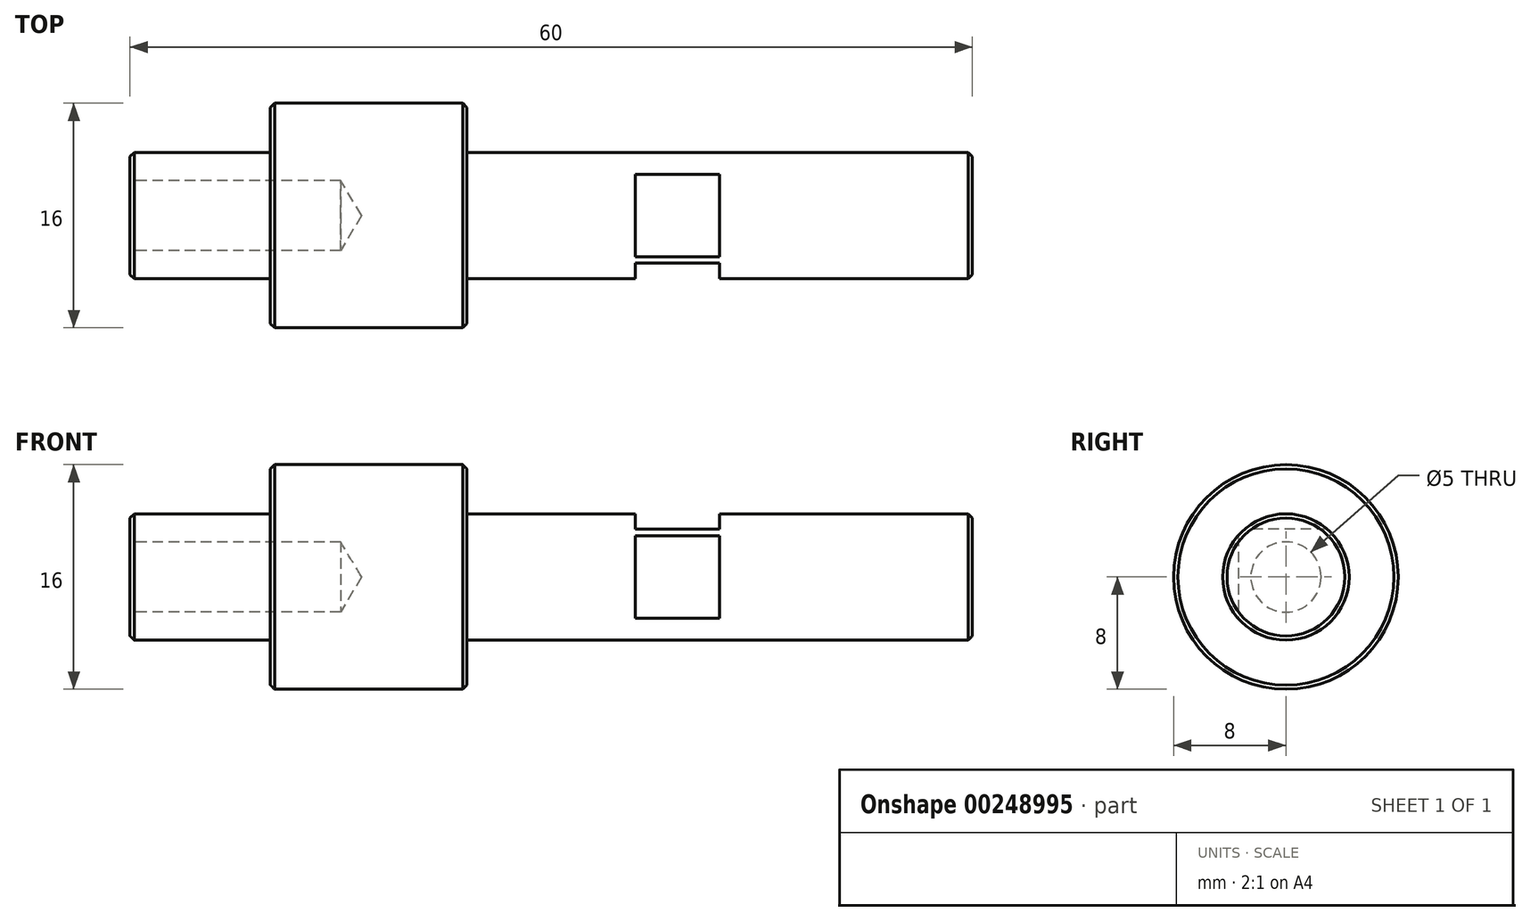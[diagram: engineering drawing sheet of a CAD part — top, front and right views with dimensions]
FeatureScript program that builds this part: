
annotation { "Feature Type Name" : "Feature", "Feature Type Description" : "" }
export const myFeature = defineFeature(function(context is Context, id is Id, definition is map)
    precondition{}
    {
        {
            var Q0;
            Q0=qCreatedBy(makeId("Front.planeOp"),FACE);
            var sketch = newSketch(context, id + "F0", { "sketchPlane" : qUnion([Q0])});
            skLineSegment(sketch, "E0", {"start": v(-26.32, 0) * mm, "end": v(33.68, 0) * mm});
            skLineSegment(sketch, "E1", {"start": v(33.68, 4.5) * mm, "end": v(33.68, 0) * mm});
            skLineSegment(sketch, "E2", {"start": v(33.68, 4.5) * mm, "end": v(-2.32, 4.5) * mm});
            skLineSegment(sketch, "E3", {"start": v(-2.32, 4.5) * mm, "end": v(-2.32, 8) * mm});
            skLineSegment(sketch, "E4", {"start": v(-2.32, 8) * mm, "end": v(-16.32, 8) * mm});
            skLineSegment(sketch, "E5", {"start": v(-16.32, 8) * mm, "end": v(-16.32, 4.5) * mm});
            skLineSegment(sketch, "E6", {"start": v(-16.32, 4.5) * mm, "end": v(-26.32, 4.5) * mm});
            skLineSegment(sketch, "E7", {"start": v(-26.32, 4.5) * mm, "end": v(-26.32, 0) * mm});
            skSolve(sketch);
        }
        {
            var Q0;
            Q0=makeQuery(id+"F0.imprint","IMPRINT",FACE,{"disambiguationData":[TD([[makeQuery(id+"F0.imprint","IMPRINT",EDGE,{"derivedFrom":sQuery(id+"F0.wireOp",EDGE,"E0")}),1.0]])]});
            var Q1;
            Q1=sQuery(id+"F0.wireOp",EDGE,"E0");
            revolve(context, id + "F1", {"entities" : qUnion([Q0]), "axis" : qUnion([Q1]), "revolveType" : RevolveType.FULL});
        }
        {
            var Q0;
            Q0=makeQuery(id+"F1.opRevolve","SWEPT_EDGE",EDGE,{"disambiguationData":[OSD([sQuery(id+"F0.wireOp",EDGE,"E1"),sQuery(id+"F0.wireOp",EDGE,"E2")])]});
            chamfer(context, id + "F2", {"entities" : qUnion([Q0]), "width" : .3 * mm, "tangentPropagation" : true});
        }
        {
            var Q0;
            Q0=makeQuery(id+"F1.opRevolve","SWEPT_FACE",FACE,{"disambiguationData":[OSD([sQuery(id+"F0.wireOp",EDGE,"E4")])]});
            chamfer(context, id + "F3", {"entities" : qUnion([Q0]), "width" : .3 * mm, "tangentPropagation" : true});
        }
        {
            var Q0;
            Q0=makeQuery(id+"F1.opRevolve","SWEPT_FACE",FACE,{"disambiguationData":[OSD([sQuery(id+"F0.wireOp",EDGE,"E7")])]});
            chamfer(context, id + "F4", {"entities" : qUnion([Q0]), "width" : .3 * mm, "tangentPropagation" : true});
        }
        {
            var Q0;
            Q0=qCreatedBy(makeId("Front.planeOp"),FACE);
            var sketch = newSketch(context, id + "F5", { "sketchPlane" : qUnion([Q0])});
            skLineSegment(sketch, "E8.bottom", {"start": v(15.68, 3) * mm, "end": v(9.68, 3) * mm});
            skLineSegment(sketch, "E8.top", {"start": v(15.68, -3) * mm, "end": v(9.68, -3) * mm});
            skLineSegment(sketch, "E8.left", {"start": v(15.68, 3) * mm, "end": v(15.68, -3) * mm});
            skLineSegment(sketch, "E8.right", {"start": v(9.68, 3) * mm, "end": v(9.68, -3) * mm});
            skPoint(sketch, "E8.middle", {"position": v(12.68, 0) * mm});
            skSolve(sketch);
        }
        {
            var Q0;
            Q0=qCreatedBy(makeId("Front.planeOp"),FACE);
            cPlane(context, id + "F6", {"entities" : qUnion([Q0]), "cplaneType" : CPlaneType.OFFSET, "offset" : 4.5 * mm, "width" : 150 * mm, "height" : 150 * mm});
        }
        {
            var Q0;
            Q0=qCreatedBy(id+"F6.planeOp",FACE);
            var sketch = newSketch(context, id + "F7", { "sketchPlane" : qUnion([Q0])});
            skPoint(sketch, "E9.0", {"position": v(15.68, 3) * mm});
            skPoint(sketch, "E10.0", {"position": v(12.68, 3) * mm});
            skLineSegment(sketch, "E11.0", {"start": v(15.68, 3) * mm, "end": v(9.68, 3) * mm});
            skPoint(sketch, "E12.0", {"position": v(9.68, 0) * mm});
            skLineSegment(sketch, "E13.0", {"start": v(15.68, -3) * mm, "end": v(9.68, -3) * mm});
            skLineSegment(sketch, "E14.0", {"start": v(15.68, 3) * mm, "end": v(15.68, -3) * mm});
            skLineSegment(sketch, "E15.0", {"start": v(9.68, 3) * mm, "end": v(9.68, -3) * mm});
            skSolve(sketch);
        }
        {
            var Q0;
            Q0=makeQuery(id+"F7.imprint","IMPRINT",FACE,{"disambiguationData":[TD([[makeQuery(id+"F7.imprint","IMPRINT",EDGE,{"derivedFrom":sQuery(id+"F7.wireOp",EDGE,"E11.0")}),1.0]])]});
            extrude(context, id + "F8", {"entities" : qUnion([Q0]), "operationType" : NewBodyOperationType.REMOVE, "oppositeDirection" : true, "depth" : 1.1 * mm});
        }
        {
            var Q0;
            Q0=qCreatedBy(makeId("Top.planeOp"),FACE);
            cPlane(context, id + "F9", {"entities" : qUnion([Q0]), "cplaneType" : CPlaneType.OFFSET, "offset" : 4.5 * mm, "width" : 150 * mm, "height" : 150 * mm});
        }
        {
            var Q0;
            Q0=qCreatedBy(id+"F9.planeOp",FACE);
            var sketch = newSketch(context, id + "F10", { "sketchPlane" : qUnion([Q0])});
            skLineSegment(sketch, "E16.bottom", {"start": v(15.68, 3) * mm, "end": v(9.68, 3) * mm});
            skLineSegment(sketch, "E16.top", {"start": v(15.68, -3) * mm, "end": v(9.68, -3) * mm});
            skLineSegment(sketch, "E16.left", {"start": v(15.68, 3) * mm, "end": v(15.68, -3) * mm});
            skLineSegment(sketch, "E16.right", {"start": v(9.68, 3) * mm, "end": v(9.68, -3) * mm});
            skPoint(sketch, "E16.middle", {"position": v(12.68, 0) * mm});
            skSolve(sketch);
        }
        {
            var Q0;
            Q0=makeQuery(id+"F10.imprint","IMPRINT",FACE,{"disambiguationData":[TD([[makeQuery(id+"F10.imprint","IMPRINT",EDGE,{"derivedFrom":sQuery(id+"F10.wireOp",EDGE,"E16.bottom")}),1.0]])]});
            extrude(context, id + "F11", {"entities" : qUnion([Q0]), "operationType" : NewBodyOperationType.REMOVE, "oppositeDirection" : true, "depth" : 1.1 * mm});
        }
        {
            var Q0;
            Q0=makeQuery(id+"F1.opRevolve","SWEPT_FACE",FACE,{"disambiguationData":[OSD([sQuery(id+"F0.wireOp",EDGE,"E7")])]});
            var sketch = newSketch(context, id + "F12", { "sketchPlane" : qUnion([Q0])});
            skPoint(sketch, "E17.0", {"position": v(0, 0) * mm});
            skSolve(sketch);
        }
        {
            var Q0;
            Q0=sQuery(id+"F12.wireOp",VERTEX,"E17.0");
            var Q1;
            Q1=makeQuery(id+"F1.opRevolve","SWEPT_BODY",BODY,{"disambiguationData":[OSD([sQuery(id+"F0.wireOp",EDGE,"E0"),sQuery(id+"F0.wireOp",EDGE,"E1"),sQuery(id+"F0.wireOp",EDGE,"E2"),sQuery(id+"F0.wireOp",EDGE,"E3"),sQuery(id+"F0.wireOp",EDGE,"E4"),sQuery(id+"F0.wireOp",EDGE,"E5"),sQuery(id+"F0.wireOp",EDGE,"E6"),sQuery(id+"F0.wireOp",EDGE,"E7")])]});
            hole(context, id + "F13", {"style" : HoleStyle.SIMPLE, "endStyle" : HoleEndStyle.BLIND, "standardTappedOrClearance" : lookupTablePath({ "standard" : "ISO", "engagement" : "75%", "pitch" : "1 mm", "size" : "M6", "type" : "Tapped" }), "standardBlindInLast" : lookupTablePath({ "standard" : "ISO", "engagement" : "75%", "pitch" : "1 mm", "size" : "M6", "type" : "Tapped" }), "holeDiameter" : 5 * mm, "showTappedDepth" : true, "holeDepth" : 15 * mm, "tappedDepth" : 12 * mm, "tapClearance" : 3, "startFromSketch" : true, "locations" : qUnion([Q0]), "scope" : qUnion([Q1]), "majorDiameter" : 6 * mm});
        }
    });
